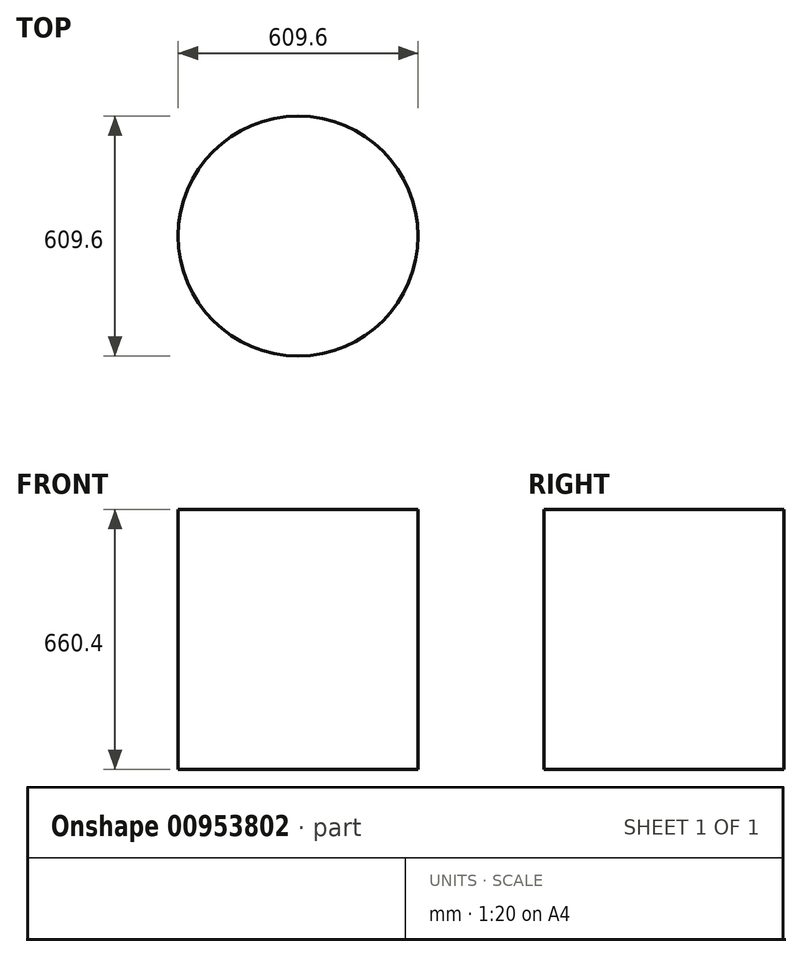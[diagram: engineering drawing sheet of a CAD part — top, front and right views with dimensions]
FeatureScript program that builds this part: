
annotation { "Feature Type Name" : "Feature", "Feature Type Description" : "" }
export const myFeature = defineFeature(function(context is Context, id is Id, definition is map)
    precondition{}
    {
        {
            var Q0;
            Q0=qCreatedBy(makeId("Top.planeOp"),FACE);
            var sketch = newSketch(context, id + "F0", { "sketchPlane" : qUnion([Q0])});
            skCircle(sketch, "E0", {"center": v(0, 0) * mm, "radius": 304.8 * mm});
            skSolve(sketch);
        }
        {
            var Q0;
            Q0 = qSketchRegion(id + "F0", true);
            extrude(context, id + "F1", {"entities" : qUnion([Q0]), "depth" : 660.4 * mm, "offsetDistance" : 25.4 * mm});
        }
    });
